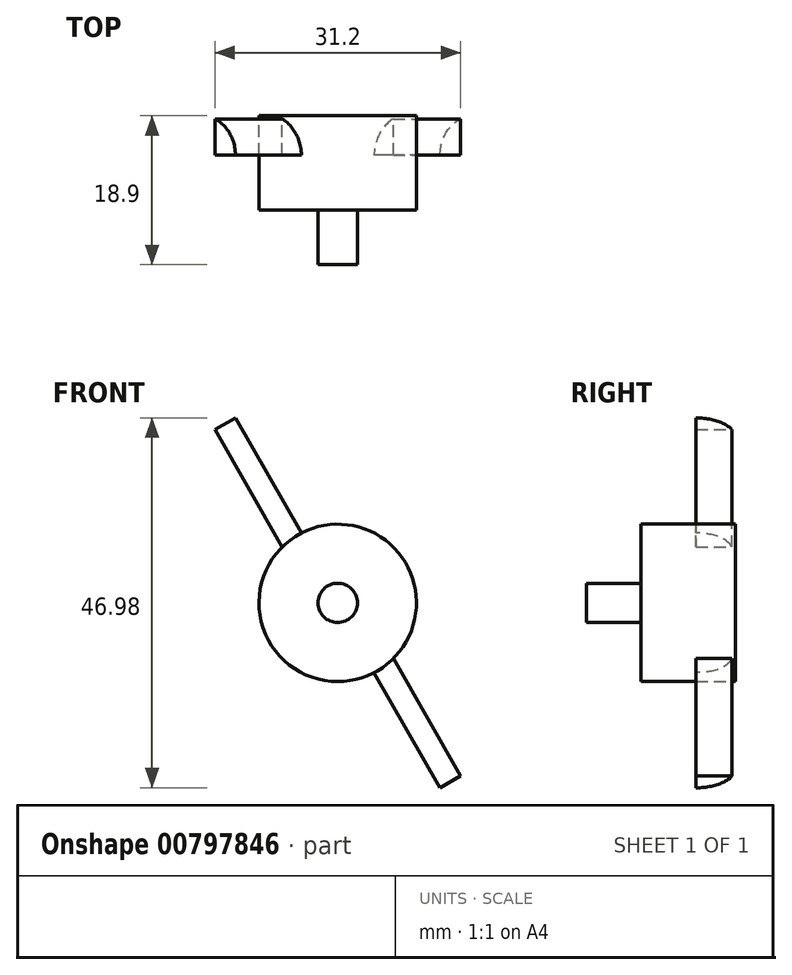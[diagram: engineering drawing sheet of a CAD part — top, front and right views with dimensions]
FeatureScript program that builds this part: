
annotation { "Feature Type Name" : "Feature", "Feature Type Description" : "" }
export const myFeature = defineFeature(function(context is Context, id is Id, definition is map)
    precondition{}
    {
        {
            var Q0;
            Q0=qCreatedBy(makeId("Front.planeOp"),FACE);
            var sketch = newSketch(context, id + "F0", { "sketchPlane" : qUnion([Q0])});
            skCircle(sketch, "E0", {"center": v(0, 0) * mm, "radius": 10 * mm});
            skSolve(sketch);
        }
        {
            var Q0;
            Q0 = qSketchRegion(id + "F0", true);
            extrude(context, id + "F1", {"entities" : qUnion([Q0]), "depth" : 12 * mm, "offsetDistance" : 25 * mm});
        }
        {
            var Q0;
            Q0=makeQuery(id+"F1.opExtrude","CAP_FACE",FACE,{"disambiguationData":[OSD([sQuery(id+"F0.wireOp",EDGE,"E0")])],"isStart":true});
            var sketch = newSketch(context, id + "F2", { "sketchPlane" : qUnion([Q0])});
            skLineSegment(sketch, "E1", {"start": v(-2.4, 5) * mm, "end": v(2.4, 5) * mm});
            skLineSegment(sketch, "E2", {"start": v(2.4, 5) * mm, "end": v(13, 23.5) * mm});
            skLineSegment(sketch, "E3", {"start": v(13, 23.5) * mm, "end": v(15.6, 22) * mm});
            skLineSegment(sketch, "E4", {"start": v(15.6, 22) * mm, "end": v(3, 0) * mm});
            skLineSegment(sketch, "E5", {"start": v(-3, 0) * mm, "end": v(3, 0) * mm});
            skLineSegment(sketch, "E6.MirrorCS", {"start": v(-3, 0) * mm, "end": v(-15.6, -22) * mm});
            skLineSegment(sketch, "E7.MirrorCS", {"start": v(-15.6, -22) * mm, "end": v(-13, -23.5) * mm});
            skLineSegment(sketch, "E8.MirrorCS", {"start": v(-13, -23.5) * mm, "end": v(-2.4, -5) * mm});
            skLineSegment(sketch, "E9.MirrorCS", {"start": v(-2.4, -5) * mm, "end": v(2.4, -5) * mm});
            skLineSegment(sketch, "E10", {"start": v(-2.4, 5) * mm, "end": v(-3, 0) * mm});
            skLineSegment(sketch, "E11", {"start": v(2.4, -5) * mm, "end": v(3, 0) * mm});
            skPoint(sketch, "E12.MirrorCS.end.orphan", {"position": v(3, 0) * mm});
            skPoint(sketch, "E13.MirrorCS.start.orphan", {"position": v(2.4, -5) * mm});
            skSolve(sketch);
        }
        {
            var Q0;
            Q0 = qSketchRegion(id + "F2", true);
            extrude(context, id + "F3", {"entities" : qUnion([Q0]), "operationType" : NewBodyOperationType.ADD, "oppositeDirection" : true, "depth" : 5 * mm, "offsetDistance" : 25 * mm});
        }
        {
            var Q0;
            Q0=makeQuery(id+"F3.opExtrude","CAP_EDGE",EDGE,{"disambiguationData":[OSD([sQuery(id+"F2.wireOp",EDGE,"E2")])],"isStart":true});
            var Q1;
            Q1=makeQuery(id+"F3.opExtrude","CAP_EDGE",EDGE,{"disambiguationData":[OSD([sQuery(id+"F2.wireOp",EDGE,"E8.MirrorCS")])],"isStart":true});
            fillet(context, id + "F4", {"entities" : qUnion([Q0, Q1]), "radius" : 5 * mm, "tangentPropagation" : true, "allowEdgeOverflow" : false});
        }
        {
            var Q0;
            Q0=makeQuery(id+"F1.opExtrude","CAP_FACE",FACE,{"disambiguationData":[OSD([sQuery(id+"F0.wireOp",EDGE,"E0")])],"isStart":false});
            var sketch = newSketch(context, id + "F5", { "sketchPlane" : qUnion([Q0])});
            skCircle(sketch, "E14", {"center": v(0, 0) * mm, "radius": 2.5 * mm});
            skSolve(sketch);
        }
        {
            var Q0;
            Q0 = qSketchRegion(id + "F5", true);
            extrude(context, id + "F6", {"entities" : qUnion([Q0]), "operationType" : NewBodyOperationType.ADD, "depth" : 6.9 * mm, "offsetDistance" : 25 * mm});
        }
    });
